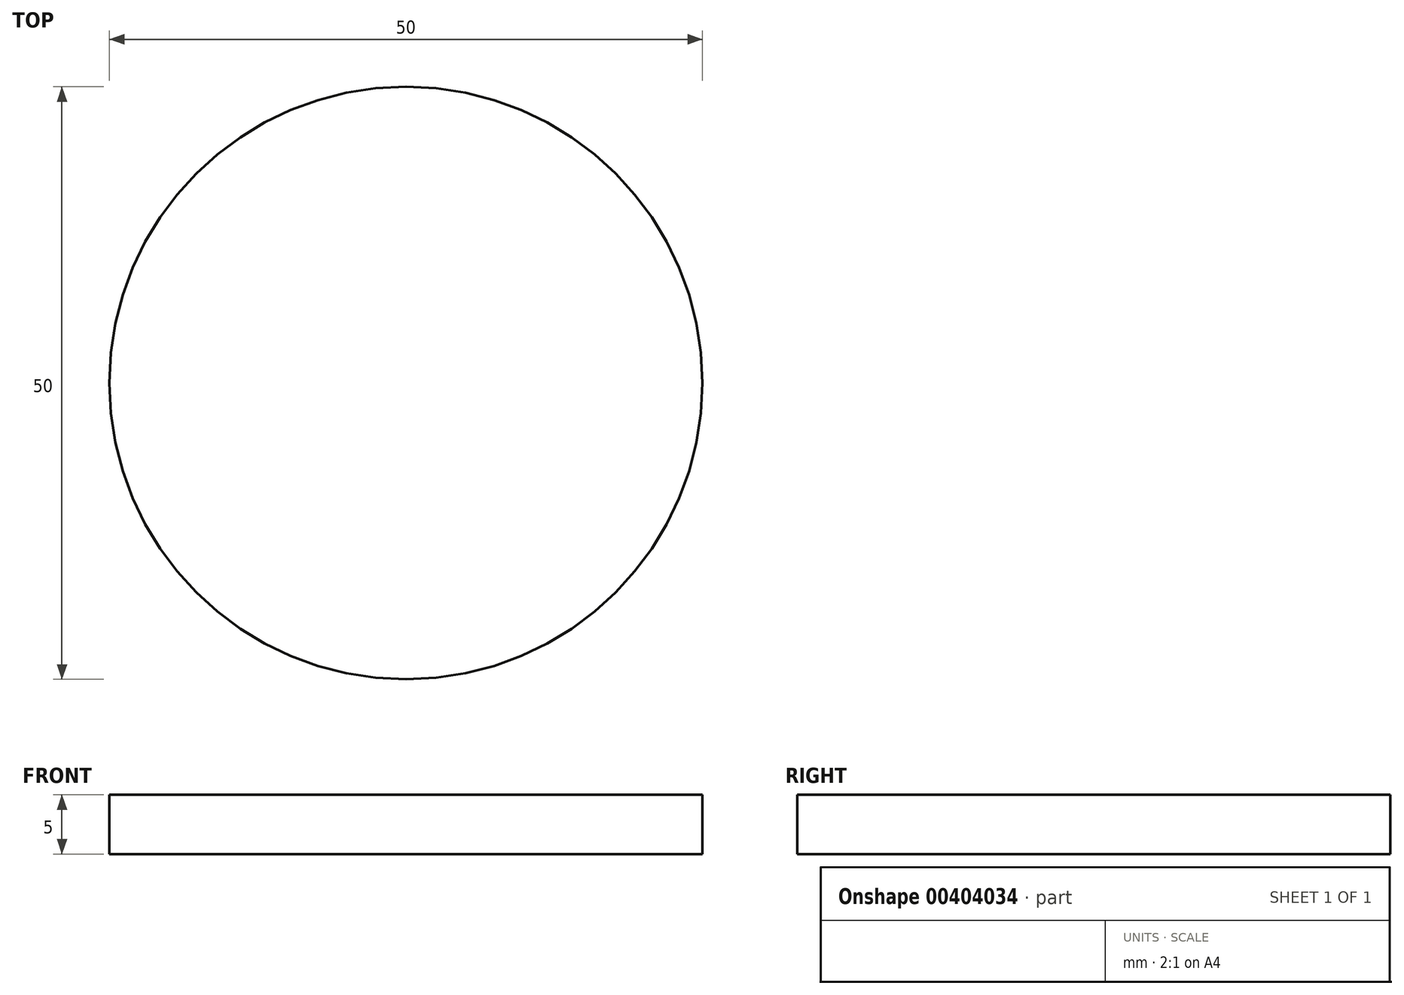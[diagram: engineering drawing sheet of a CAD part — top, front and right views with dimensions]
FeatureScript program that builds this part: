
annotation { "Feature Type Name" : "Feature", "Feature Type Description" : "" }
export const myFeature = defineFeature(function(context is Context, id is Id, definition is map)
    precondition{}
    {
        {
            var Q0;
            Q0=qCreatedBy(makeId("Top.planeOp"),FACE);
            var sketch = newSketch(context, id + "F0", { "sketchPlane" : qUnion([Q0])});
            skCircle(sketch, "E0", {"center": v(0, 0) * mm, "radius": 25 * mm});
            skSolve(sketch);
        }
        {
            var Q0;
            Q0=makeQuery(id+"F0.imprint","IMPRINT",FACE,{"disambiguationData":[TD([[makeQuery(id+"F0.imprint","IMPRINT",EDGE,{"derivedFrom":sQuery(id+"F0.wireOp",EDGE,"E0")}),1.0]])]});
            extrude(context, id + "F1", {"entities" : qUnion([Q0]), "depth" : 5 * mm});
        }
    });
